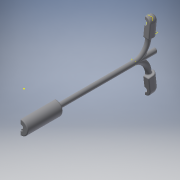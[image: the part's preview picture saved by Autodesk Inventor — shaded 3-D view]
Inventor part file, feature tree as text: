
AUTODESK INVENTOR PART (.ipt)
format: ipt  version: 2018 (Build 220112000, 112)  size: 562,176 bytes
history: native  units: mm
features: sketch x11, extrude x9, fillet x6, plane x3, projected_geometry x3, revolve x1, sweep x1, mirror x1
ambient origin geometry x8: Origin, YZ Plane, XZ Plane, XY Plane, X Axis, Y Axis, Z Axis, Center Point
bodies: Solid1 (feature_tree)
feature tree (35):
  revolve  "Revolution1"  [1 undecoded]
  fillet  "Fillet1"  Radius=8.0mm
  fillet  "Fillet2"  Radius=40.0mm
  fillet  "Fillet3"  [1 undecoded]
  plane  "Work Plane1"
  sweep  "Sweep1"
  extrude  "Extrusion2"  Depth=1.0mm
  fillet  "Fillet4"  Radius=1.0mm
  fillet  "Fillet5"  Radius=1.0mm
  extrude  "Extrusion3"  Depth=1.0mm
  extrude  "Extrusion4"  Depth=6.601018mm
  extrude  "Extrusion5"  Depth=1.0mm
  extrude  "Extrusion6"  [1 undecoded]
  extrude  "Extrusion7"  Depth=18.0mm
  plane  "Work Plane3"
  extrude  "Extrusion8"  TaperAngle=0.0deg  [1 undecoded]
  extrude  "Extrusion9"  Depth=5.0mm
  plane  "Work Plane4"
  extrude  "Extrusion10"  Depth=6.0mm
  fillet  "Fillet6"  Radius=20.0mm
  mirror  "Mirror2"
  sketch  "Sketch6"  dims[d0=150.0mm d1=3.0mm d3=8.0mm d4=40.0mm d5=90.0deg]
  sketch  "Sketch8"  dims[d20=1.5mm d21=1.5mm]
  sketch  "Sketch9"  dims[d22=1.5mm d23=1.0mm d24=1.0mm d25=1.0mm]
  projected_geometry  "Projected Loop3"
  sketch  "Sketch10"  dims[d26=1.0mm d27=1.0mm]
  projected_geometry  "Projected Loop4"
  sketch  "Sketch11"  dims[d28=1.456552mm d29=6.601018mm]
  sketch  "Sketch12"  dims[d30=2.0mm d31=1.0mm]
  sketch  "Sketch13"  dims[d32=1.0mm d33=-23.0mm]
  sketch  "Sketch14"  dims[d38=18.0mm d39=18.0mm]
  sketch  "Sketch15"  dims[d40=16.0mm d41=0.0mm d42=0.0mm]
  projected_geometry  "Projected Loop5"
  sketch  "Sketch16"  dims[d43=12.0mm d44=5.0mm]
  sketch  "Sketch17"  dims[d45=6.0mm d46=6.0mm d47=20.0mm d48=0.0mm d49=6.0mm d50=1.0mm d51=3.0mm d52=5.5mm d53=8.0mm d54=0.0mm d55=10.0mm d56=0.0mm d57=50.0mm d58=0.0mm d59=1.4mm d60=0.0mm d61=4.332171mm d62=15.0mm d63=0.0mm d64=-3.0mm d65=6.5mm d66=1.1mm d67=0.0mm d68=10.0mm d69=0.0mm d70=-3.0mm d71=10.0mm d72=0.0mm d73=0.5mm]
note: 4 required parameter values undecoded (feature->parameter linkage not recoverable at this tier; creation-order binding heuristic only, values carry confidence <= 0.55)